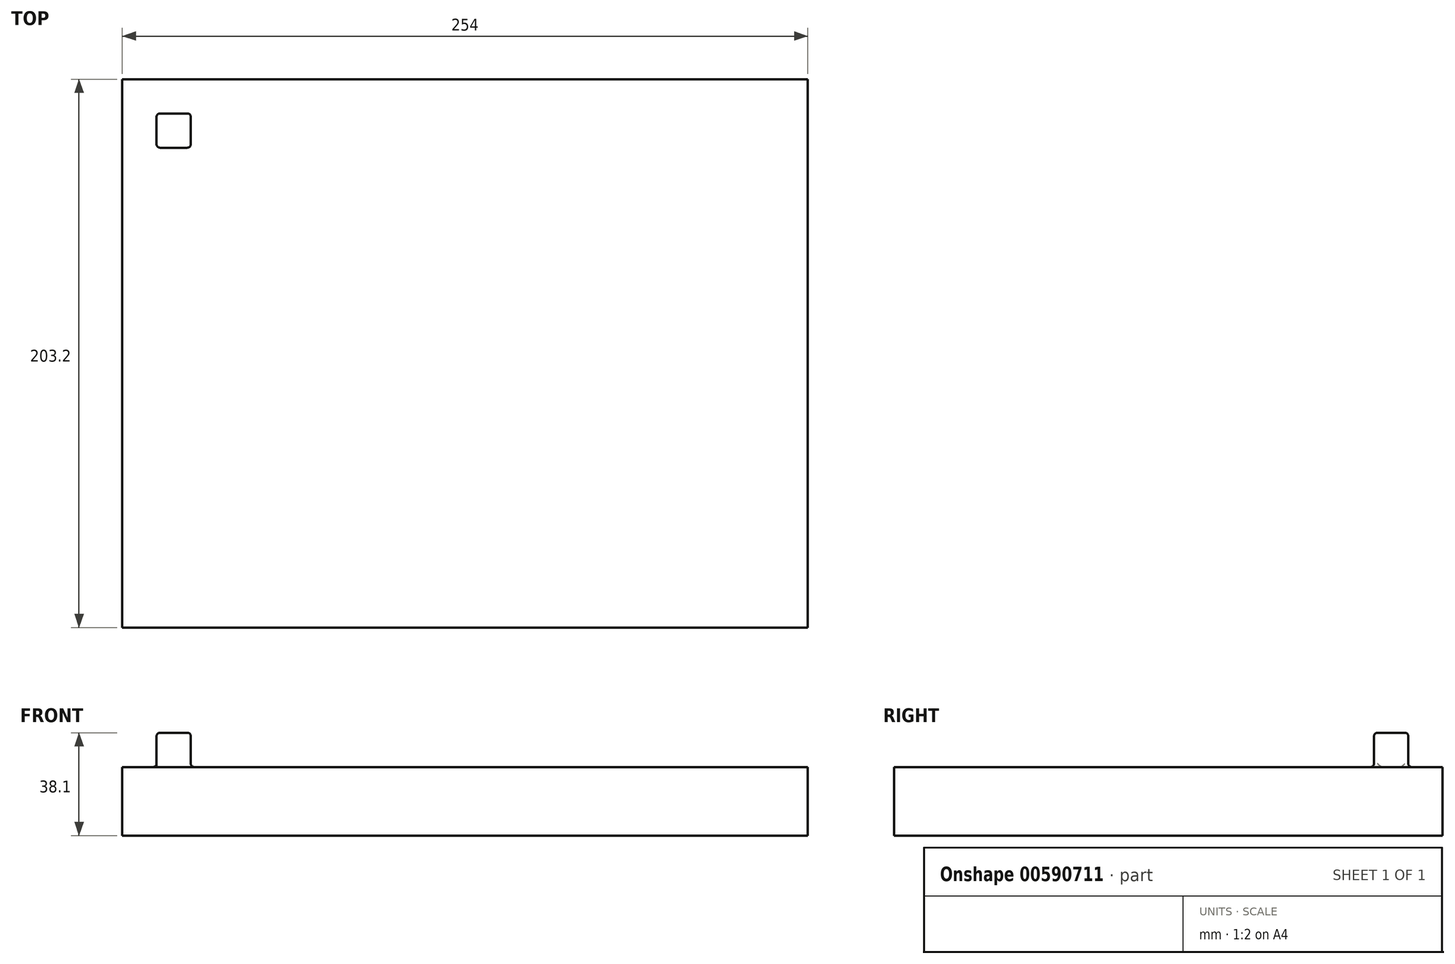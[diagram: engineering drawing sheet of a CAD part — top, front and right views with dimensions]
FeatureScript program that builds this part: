
annotation { "Feature Type Name" : "Feature", "Feature Type Description" : "" }
export const myFeature = defineFeature(function(context is Context, id is Id, definition is map)
    precondition{}
    {
        {
            var Q0;
            Q0=qCreatedBy(makeId("Top.planeOp"),FACE);
            var sketch = newSketch(context, id + "F0", { "sketchPlane" : qUnion([Q0])});
            skLineSegment(sketch, "E0.bottom", {"start": v(0, 0) * mm, "end": v(254, 0) * mm});
            skLineSegment(sketch, "E0.top", {"start": v(0, 203.2) * mm, "end": v(254, 203.2) * mm});
            skLineSegment(sketch, "E0.left", {"start": v(0, 0) * mm, "end": v(0, 203.2) * mm});
            skLineSegment(sketch, "E0.right", {"start": v(254, 0) * mm, "end": v(254, 203.2) * mm});
            skSolve(sketch);
        }
        {
            var Q0;
            Q0=makeQuery(id+"F0.imprint","IMPRINT",FACE,{"disambiguationData":[TD([[makeQuery(id+"F0.imprint","IMPRINT",EDGE,{"derivedFrom":sQuery(id+"F0.wireOp",EDGE,"E0.bottom")}),1.0]])]});
            extrude(context, id + "F1", {"entities" : qUnion([Q0]), "depth" : 25.4 * mm, "offsetDistance" : 25.4 * mm});
        }
        {
            var Q0;
            Q0=makeQuery(id+"F1.opExtrude","CAP_FACE",FACE,{"disambiguationData":[OSD([sQuery(id+"F0.wireOp",EDGE,"E0.bottom"),sQuery(id+"F0.wireOp",EDGE,"E0.top"),sQuery(id+"F0.wireOp",EDGE,"E0.left"),sQuery(id+"F0.wireOp",EDGE,"E0.right")])],"isStart":false});
            var sketch = newSketch(context, id + "F2", { "sketchPlane" : qUnion([Q0])});
            skLineSegment(sketch, "E1.bottom", {"start": v(12.7, 190.5) * mm, "end": v(25.4, 190.5) * mm});
            skLineSegment(sketch, "E1.top", {"start": v(12.7, 177.8) * mm, "end": v(25.4, 177.8) * mm});
            skLineSegment(sketch, "E1.left", {"start": v(12.7, 190.5) * mm, "end": v(12.7, 177.8) * mm});
            skLineSegment(sketch, "E1.right", {"start": v(25.4, 190.5) * mm, "end": v(25.4, 177.8) * mm});
            skSolve(sketch);
        }
        {
            var Q0;
            Q0=makeQuery(id+"F2.imprint","IMPRINT",FACE,{"disambiguationData":[TD([[makeQuery(id+"F2.imprint","IMPRINT",EDGE,{"derivedFrom":sQuery(id+"F2.wireOp",EDGE,"E1.bottom")}),-1.0]])]});
            extrude(context, id + "F3", {"entities" : qUnion([Q0]), "operationType" : NewBodyOperationType.ADD, "depth" : 12.7 * mm, "offsetDistance" : 25.4 * mm});
        }
        {
            var Q0;
            Q0=makeQuery(id+"F3.opExtrude","CAP_EDGE",EDGE,{"disambiguationData":[OSD([sQuery(id+"F2.wireOp",EDGE,"E1.top")])],"isStart":true});
            var Q1;
            Q1=makeQuery(id+"F3.opExtrude","CAP_EDGE",EDGE,{"disambiguationData":[OSD([sQuery(id+"F2.wireOp",EDGE,"E1.right")])],"isStart":true});
            var Q2;
            Q2=makeQuery(id+"F3.opExtrude","CAP_EDGE",EDGE,{"disambiguationData":[OSD([sQuery(id+"F2.wireOp",EDGE,"E1.bottom")])],"isStart":true});
            var Q3;
            Q3=makeQuery(id+"F3.opExtrude","CAP_EDGE",EDGE,{"disambiguationData":[OSD([sQuery(id+"F2.wireOp",EDGE,"E1.left")])],"isStart":true});
            var Q4;
            Q4=makeQuery(id+"F3.opExtrude","CAP_FACE",FACE,{"disambiguationData":[OSD([sQuery(id+"F2.wireOp",EDGE,"E1.bottom"),sQuery(id+"F2.wireOp",EDGE,"E1.top"),sQuery(id+"F2.wireOp",EDGE,"E1.left"),sQuery(id+"F2.wireOp",EDGE,"E1.right")])],"isStart":false});
            var Q5;
            Q5=makeQuery(id+"F3.opExtrude","SWEPT_FACE",FACE,{"disambiguationData":[OSD([sQuery(id+"F2.wireOp",EDGE,"E1.top")])]});
            var Q6;
            Q6=makeQuery(id+"F3.opExtrude","SWEPT_FACE",FACE,{"disambiguationData":[OSD([sQuery(id+"F2.wireOp",EDGE,"E1.right")])]});
            var Q7;
            Q7=makeQuery(id+"F3.opExtrude","SWEPT_FACE",FACE,{"disambiguationData":[OSD([sQuery(id+"F2.wireOp",EDGE,"E1.bottom")])]});
            var Q8;
            Q8=makeQuery(id+"F3.opExtrude","SWEPT_EDGE",EDGE,{"disambiguationData":[OSD([sQuery(id+"F2.wireOp",EDGE,"E1.top"),sQuery(id+"F2.wireOp",EDGE,"E1.left")])]});
            fillet(context, id + "F4", {"entities" : qUnion([Q0, Q1, Q2, Q3, Q4, Q5, Q6, Q7, Q8]), "radius" : 1.27 * mm, "tangentPropagation" : true, "allowEdgeOverflow" : false});
        }
    });
